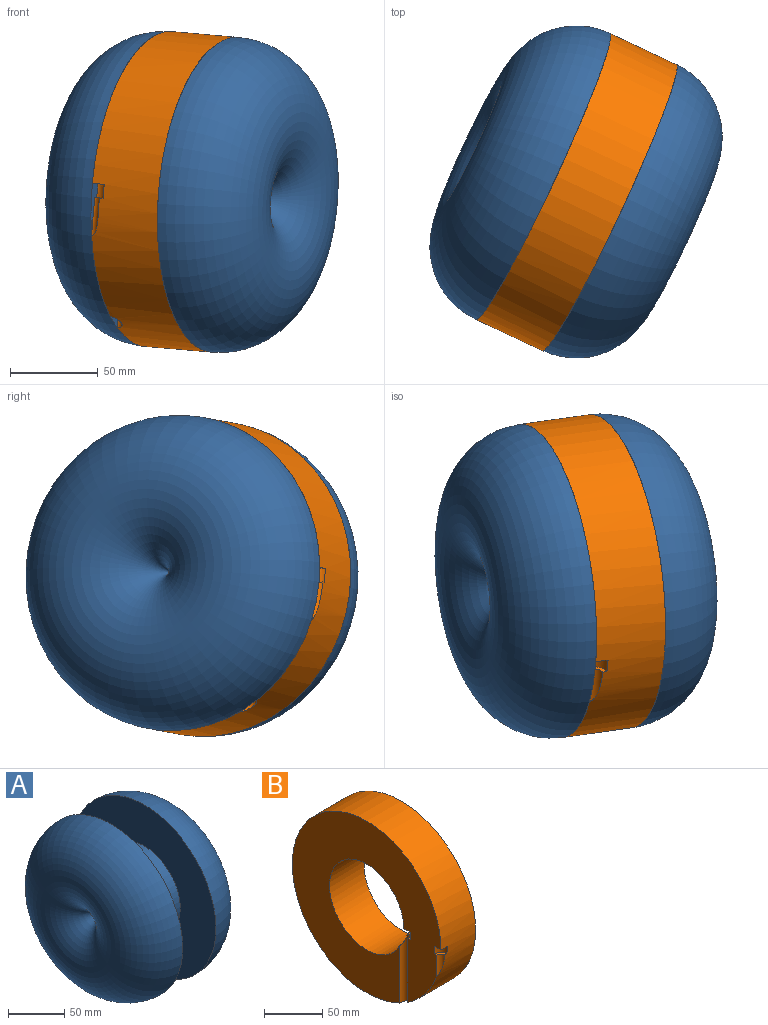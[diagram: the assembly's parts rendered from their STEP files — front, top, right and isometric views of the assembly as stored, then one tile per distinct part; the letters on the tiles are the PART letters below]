
ASSEMBLY  parts=2 mates=1
PART A: 5 faces, bbox 131.9x194.8x194.8 mm
  f0: torus R=45mm, axis (1,0,0), area 39971.9mm2, adj f4
  f1: torus R=45mm, axis (1,0,0), area 39971.9mm2, adj f2
  f2: plane 180x180mm, normal (1,0,0), area 19085.2mm2, adj f1,f3
  f3: cylinder r=45mm len=90mm, axis (1,0,0), area 11848.6mm2, adj f2,f4
  f4: plane 180x180mm, normal (-1,0,0), area 19085.2mm2, adj f0,f3
PART B: 12 faces, bbox 41.9x180x180 mm
  f0: cylinder r=90mm len=180mm, axis (-1,0,0), area 23500.4mm2, adj f1,f3,f4,f8,f9,f10,f11
  f1: plane 180x180mm, normal (-1,0,0), area 18236.8mm2, adj f0,f2,f4,f5,f6,f7,f8,f9
  f2: cylinder r=45mm len=90mm, axis (-1,0,0), area 11735.1mm2, adj f1,f3,f4,f5,f6,f7
  f3: plane 180x180mm, normal (1,0,0), area 19085.2mm2, adj f0,f2
  f4: cylinder r=5mm len=72.62mm, axis (0,0,1), area 1033.4mm2, adj f0,f1,f2,f5
  f5: plane 8.22x7.5mm, normal (0,0,1), area 26.3mm2, adj f1,f2,f4,f6
  f6: cylinder r=7.5mm len=8.22mm, axis (0,0,1), area 96.2mm2, adj f1,f2,f5,f7
  f7: plane 7.5x7.5mm, normal (0,0,-1), area 44.2mm2, adj f1,f2,f6
  f8: cylinder r=5mm len=21.58mm, axis (0,0,1), area 116mm2, adj f0,f1,f9
  f9: plane 7.49x7.14mm, normal (0,0,1), area 23.7mm2, adj f0,f1,f8,f10
  f10: cylinder r=7.5mm len=8mm, axis (0,0,1), area 93.3mm2, adj f0,f1,f9,f11
  f11: plane 7.5x7.5mm, normal (0,0,-1), area 44.2mm2, adj f0,f1,f10
PLACE A rot(axis=(-0.04,0.19,-0.98),25.5deg) t=(-34.54,-161.41,15.29)mm
PLACE B rot(axis=(-0.04,0.19,-0.98),25.5deg) t=(-34.54,-161.41,15.29)mm
MATE revolute B.f0 <-> A.f0  axis (-0.9,0.42,0.08) through (-6.12,-100.23,12.81)mm
